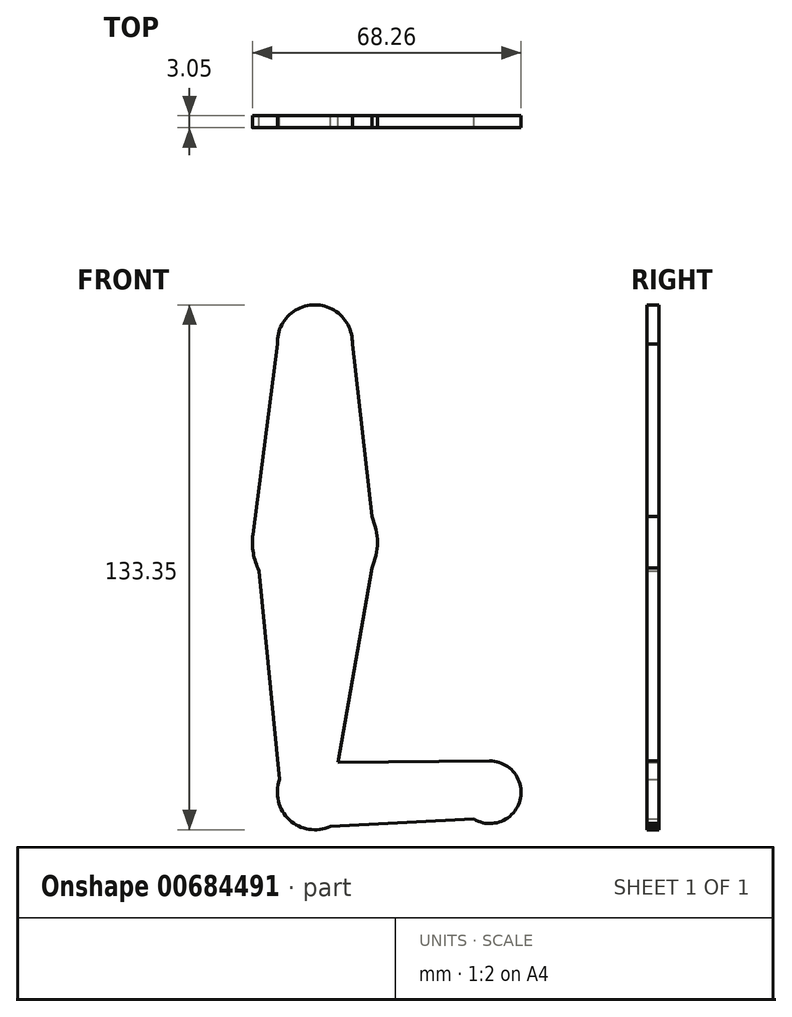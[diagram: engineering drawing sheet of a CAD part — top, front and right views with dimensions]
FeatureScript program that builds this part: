
annotation { "Feature Type Name" : "Feature", "Feature Type Description" : "" }
export const myFeature = defineFeature(function(context is Context, id is Id, definition is map)
    precondition{}
    {
        {
            var Q0;
            Q0=qCreatedBy(makeId("Front.planeOp"),FACE);
            var sketch = newSketch(context, id + "F0", { "sketchPlane" : qUnion([Q0])});
            skLineSegment(sketch, "E0", {"start": v(0, 0) * mm, "end": v(0, 63.5) * mm});
            skCircle(sketch, "E1", {"center": v(0, 63.5) * mm, "radius": 15.88 * mm});
            skLineSegment(sketch, "E2", {"start": v(0, 63.5) * mm, "end": v(0, 114.3) * mm});
            skCircle(sketch, "E3", {"center": v(0, 114.3) * mm, "radius": 9.53 * mm});
            skCircle(sketch, "E4", {"center": v(0, 0) * mm, "radius": 9.53 * mm});
            skLineSegment(sketch, "E5", {"start": v(0, 0) * mm, "end": v(44.45, 0) * mm});
            skCircle(sketch, "E6", {"center": v(44.45, 0) * mm, "radius": 7.94 * mm});
            skLineSegment(sketch, "E7", {"start": v(-9.52, 113.87) * mm, "end": v(-15.74, 65.53) * mm});
            skLineSegment(sketch, "E8", {"start": v(-15.74, 65.53) * mm, "end": v(-9.52, 113.87) * mm});
            skLineSegment(sketch, "E9", {"start": v(9.52, 113.87) * mm, "end": v(14.47, 70.03) * mm});
            skLineSegment(sketch, "E10", {"start": v(14.47, 70.03) * mm, "end": v(9.52, 113.87) * mm});
            skLineSegment(sketch, "E11", {"start": v(14.47, 56.97) * mm, "end": v(5.83, 7.53) * mm});
            skLineSegment(sketch, "E12", {"start": v(5.83, 7.53) * mm, "end": v(14.47, 56.97) * mm});
            skLineSegment(sketch, "E13", {"start": v(5.83, 7.53) * mm, "end": v(44.37, 7.94) * mm});
            skLineSegment(sketch, "E14", {"start": v(44.37, 7.94) * mm, "end": v(5.83, 7.53) * mm});
            skLineSegment(sketch, "E15", {"start": v(3.97, -8.66) * mm, "end": v(40.4, -6.82) * mm});
            skLineSegment(sketch, "E16", {"start": v(40.4, -6.82) * mm, "end": v(3.97, -8.66) * mm});
            skLineSegment(sketch, "E17", {"start": v(-14.13, 56.27) * mm, "end": v(-8.96, 3.23) * mm});
            skLineSegment(sketch, "E18", {"start": v(-8.96, 3.23) * mm, "end": v(-14.13, 56.27) * mm});
            skSolve(sketch);
        }
        {
            var Q0;
            Q0 = qSketchRegion(id + "F0", true);
            extrude(context, id + "F1", {"entities" : qUnion([Q0]), "depth" : 3.05 * mm, "offsetDistance" : 25.4 * mm});
        }
    });
